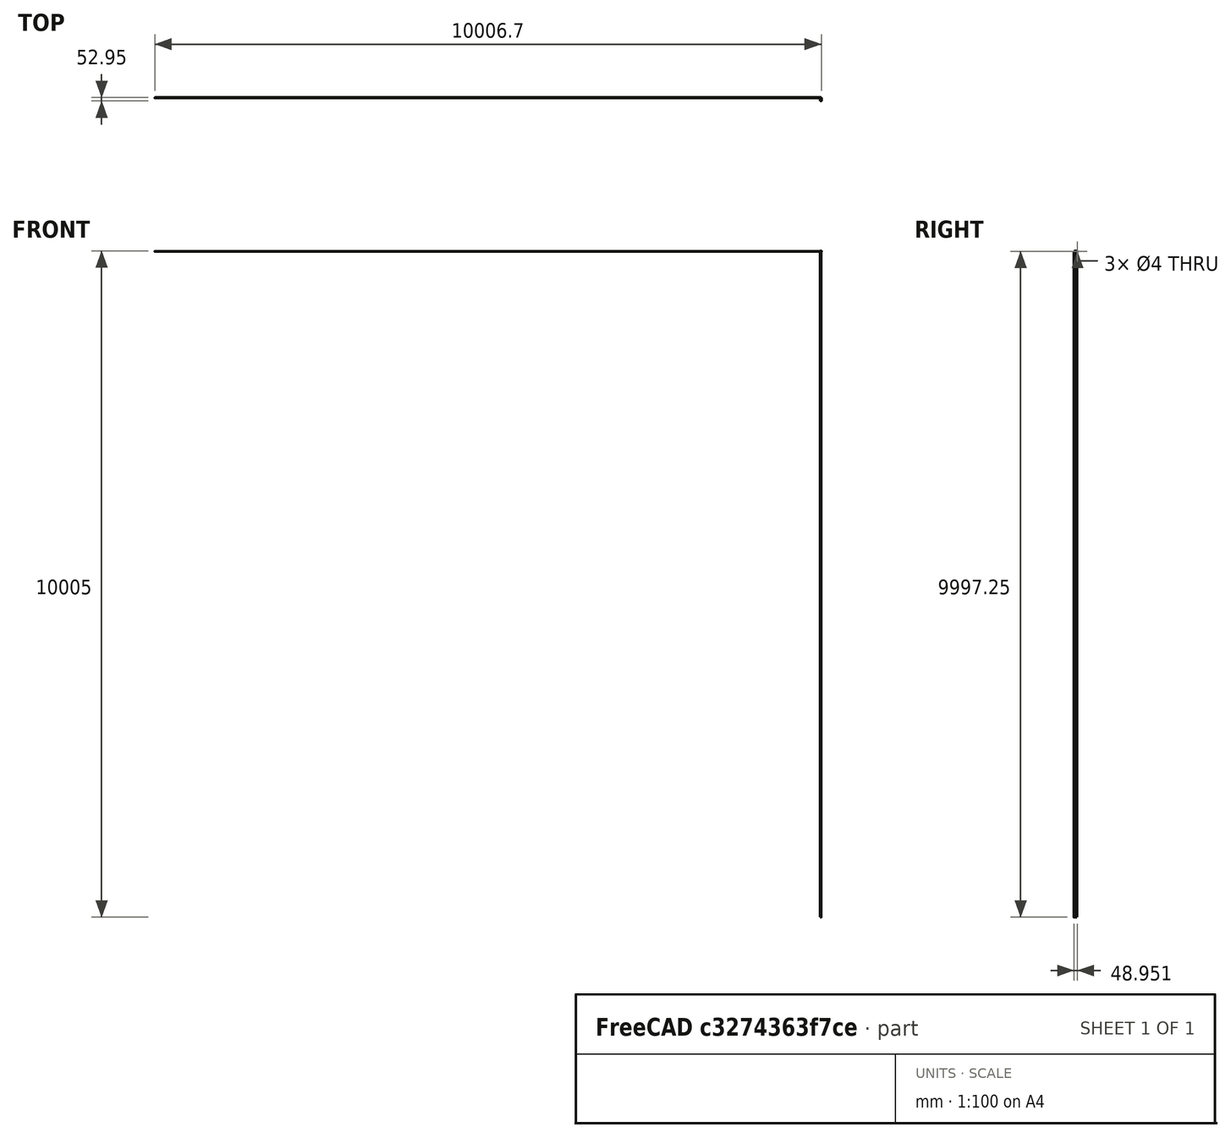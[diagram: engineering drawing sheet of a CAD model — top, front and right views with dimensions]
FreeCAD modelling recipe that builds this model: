
FCSTD DOCUMENT  (FreeCAD 0.14R3702 (Git))
Label: idler
License: CC-BY 3.0
LicenseURL: http://creativecommons.org/licenses/by/3.0/
objects: Sketcher::SketchObject×11, PartDesign::Pocket×7, PartDesign::Pad×4, PartDesign::Chamfer×2, Mesh::Feature×1, PartDesign::Fillet×1
note: 36 computed .brp shape members not serialized (recipe doc carries the construction recipe); baked Part::Feature solids carry a one-line shape summary decoded from their .brp

FEATURE [Mesh::Feature] idler1_long
  Placement = pos=(0,0,11) rot=(0,0,1;0rad)
FEATURE [Sketcher::SketchObject] Sketch
  sketch-geometry (4):
    g0: LineSegment StartX=-19.5 StartY=43.9769 StartZ=0 EndX=0 EndY=43.9769 EndZ=0
    g1: LineSegment StartX=0 StartY=43.9769 StartZ=0 EndX=0 EndY=5.97689 EndZ=0
    g2: LineSegment StartX=0 StartY=5.97689 StartZ=0 EndX=-19.5 EndY=5.97689 EndZ=0
    g3: LineSegment StartX=-19.5 StartY=5.97689 StartZ=0 EndX=-19.5 EndY=43.9769 EndZ=0
  constraints (11):
    c: Coincident(g0,g1)
    c: Coincident(g1,g2)
    c: Coincident(g2,g3)
    c: Coincident(g3,g0)
    c: Horizontal(g0)
    c: Horizontal(g2)
    c: Vertical(g1)
    c: Vertical(g3)
    c: PointOnObject(g0,g-2)
    c: DistanceY(g3) = 38
    c: DistanceX(g0) = 19.5
FEATURE [PartDesign::Pad] Pad
  Length = 8.5
  Length2 = 100
  Sketch = -> Sketch
  Type = 0
FEATURE [Sketcher::SketchObject] Sketch001
  Placement = pos=(0,0,8.5) rot=(0,0,1;0rad)
  Support = -> Pad [Face6]
  sketch-geometry (4):
    g0: LineSegment StartX=-15 StartY=41.4603 StartZ=0 EndX=-5 EndY=41.4603 EndZ=0
    g1: LineSegment StartX=-5 StartY=41.4603 StartZ=0 EndX=-5 EndY=18.4941 EndZ=0
    g2: LineSegment StartX=-5 StartY=18.4941 StartZ=0 EndX=-15 EndY=18.4941 EndZ=0
    g3: LineSegment StartX=-15 StartY=18.4941 StartZ=0 EndX=-15 EndY=41.4603 EndZ=0
  constraints (10):
    c: Coincident(g0,g1)
    c: Coincident(g1,g2)
    c: Coincident(g2,g3)
    c: Coincident(g3,g0)
    c: Horizontal(g0)
    c: Horizontal(g2)
    c: Vertical(g1)
    c: Vertical(g3)
    c: DistanceX(g0) = -5
    c: DistanceX(g0) = 10
FEATURE [PartDesign::Pocket] Pocket
  Length = 5
  Sketch = -> Sketch001
  Type = 1
FEATURE [Sketcher::SketchObject] Sketch002
  Placement = pos=(0,0,8.5) rot=(0,0,1;0rad)
  Support = -> Pocket [Face5]
  sketch-geometry (4):
    g0: LineSegment StartX=-19.9255 StartY=18.8051 StartZ=0 EndX=0.686893 EndY=18.8051 EndZ=0
    g1: LineSegment StartX=0.686893 StartY=18.8051 StartZ=0 EndX=0.686893 EndY=5.03095 EndZ=0
    g2: LineSegment StartX=0.686893 StartY=5.03095 StartZ=0 EndX=-19.9255 EndY=5.03095 EndZ=0
    g3: LineSegment StartX=-19.9255 StartY=5.03095 StartZ=0 EndX=-19.9255 EndY=18.8051 EndZ=0
  constraints (8):
    c: Coincident(g0,g1)
    c: Coincident(g1,g2)
    c: Coincident(g2,g3)
    c: Coincident(g3,g0)
    c: Horizontal(g0)
    c: Horizontal(g2)
    c: Vertical(g1)
    c: Vertical(g3)
FEATURE [PartDesign::Pocket] Pocket001
  Length = 1.5
  Sketch = -> Sketch002
  Type = 0
FEATURE [Sketcher::SketchObject] Sketch003
  Placement = pos=(0,0,7) rot=(0,0,1;0rad)
  Support = -> Pocket001 [Face7]
  sketch-geometry (4):
    g0: ArcOfCircle CenterX=-5.11958 CenterY=13.125 CenterZ=0 NormalX=0 NormalY=0 NormalZ=1 Radius=2.6 StartAngle=1.234e-08 EndAngle=3.14159
    g1: ArcOfCircle CenterX=-5.11958 CenterY=1.62771 CenterZ=0 NormalX=0 NormalY=0 NormalZ=1 Radius=2.6 StartAngle=3.14159 EndAngle=6.28319
    g2: LineSegment StartX=-7.71958 StartY=13.125 StartZ=0 EndX=-7.71958 EndY=1.62771 EndZ=0
    g3: LineSegment StartX=-2.51958 StartY=13.125 StartZ=0 EndX=-2.51958 EndY=1.62771 EndZ=0
  constraints (11):
    c: Tangent(g0,g2)
    c: Tangent(g0,g3)
    c: Tangent(g1,g2)
    c: Tangent(g1,g3)
    c: Coincident(g0,g3)
    c: Coincident(g0,g2)
    c: Coincident(g2,g1)
    c: Coincident(g3,g1)
    c: Vertical(g2)
    c: Equal(g0,g1)
    c: Radius(g1) = 2.6
FEATURE [PartDesign::Pocket] Pocket002
  Length = 5
  Sketch = -> Sketch003
  Type = 1
FEATURE [Sketcher::SketchObject] Sketch004
  Placement = pos=(0,43.9769,0) rot=(0,0.707107,0.707107;3.14159rad)
  Support = -> Pocket002 [Face1]
  sketch-geometry (4):
    g0: LineSegment StartX=6 StartY=8.5 StartZ=0 EndX=10.5 EndY=8.5 EndZ=0
    g1: LineSegment StartX=10.5 StartY=8.5 StartZ=0 EndX=10.5 EndY=0 EndZ=0
    g2: LineSegment StartX=10.5 StartY=0 StartZ=0 EndX=6 EndY=0 EndZ=0
    g3: LineSegment StartX=6 StartY=0 StartZ=0 EndX=6 EndY=8.5 EndZ=0
  constraints (11):
    c: Coincident(g0,g1)
    c: Coincident(g1,g2)
    c: Coincident(g2,g3)
    c: Coincident(g3,g0)
    c: Horizontal(g0)
    c: Horizontal(g2)
    c: Vertical(g1)
    c: Vertical(g3)
    c: PointOnObject(g1,g-1)
    c: DistanceX(g0) = 4.5
    c: DistanceX(g0) = 6
FEATURE [PartDesign::Pad] Pad001
  Length = 8
  Length2 = 100
  Sketch = -> Sketch004
  Type = 0
FEATURE [Sketcher::SketchObject] Sketch005
  ExternalGeometry = -> [Pad001]
  Placement = pos=(-6,0,0) rot=(0.57735,0.57735,0.57735;2.0944rad)
  Support = -> Pad001 [Face23]
  sketch-geometry (1):
    g0: Circle CenterX=47.9813 CenterY=4.25 CenterZ=0 NormalX=0 NormalY=0 NormalZ=1 Radius=2
  constraints (2):
    c: Radius(g0) = 2
    c: Distance(g0,g-3) = 4.25
FEATURE [PartDesign::Pocket] Pocket003
  Length = 5
  Sketch = -> Sketch005
  Type = 1
FEATURE [Sketcher::SketchObject] Sketch006
  Placement = pos=(0,0,0) rot=(0.57735,0.57735,0.57735;2.0944rad)
  Support = -> Pocket003 [Face11]
  sketch-geometry (2):
    g0: ArcOfCircle CenterX=30 CenterY=4 CenterZ=0 NormalX=0 NormalY=0 NormalZ=1 Radius=8 StartAngle=5.75959 EndAngle=9.94838
    g1: LineSegment StartX=23.0718 StartY=0 StartZ=0 EndX=36.9282 EndY=0 EndZ=0
  constraints (7):
    c: Radius(g0) = 8
    c: DistanceX(g0) = 30
    c: DistanceY(g0) = 4
    c: Coincident(g1,g0)
    c: Coincident(g1,g0)
    c: PointOnObject(g0,g-1)
    c: PointOnObject(g0,g-1)
FEATURE [PartDesign::Pad] Pad002
  Length = 6.4
  Length2 = 100
  Reversed = true
  Sketch = -> Sketch006
  Type = 0
FEATURE [Sketcher::SketchObject] Sketch007
  Placement = pos=(-19.5,0,0) rot=(0.57735,-0.57735,-0.57735;2.0944rad)
  Support = -> Pad002 [Face1]
  sketch-geometry (2):
    g0: ArcOfCircle CenterX=-30 CenterY=4 CenterZ=0 NormalX=0 NormalY=0 NormalZ=1 Radius=8 StartAngle=5.75959 EndAngle=9.94838
    g1: LineSegment StartX=-36.9282 StartY=0 StartZ=0 EndX=-23.0718 EndY=0 EndZ=0
  constraints (7):
    c: Radius(g0) = 8
    c: DistanceX(g0) = -30
    c: DistanceY(g0) = 4
    c: Coincident(g1,g0)
    c: Coincident(g1,g0)
    c: PointOnObject(g0,g-1)
    c: PointOnObject(g0,g-1)
FEATURE [PartDesign::Pad] Pad003
  Length = 6
  Length2 = 100
  Reversed = true
  Sketch = -> Sketch007
  Type = 0
FEATURE [Sketcher::SketchObject] Sketch008
  Placement = pos=(-13.5,0,0) rot=(0.57735,0.57735,0.57735;2.0944rad)
  Support = -> Pad003 [Face22]
  sketch-geometry (5):
    g0: ArcOfCircle CenterX=30 CenterY=4.25 CenterZ=0 NormalX=0 NormalY=0 NormalZ=1 Radius=4 StartAngle=5.83037 EndAngle=9.87759
    g1: LineSegment [constr] StartX=33.5969 StartY=2.5 StartZ=0 EndX=26.4031 EndY=2.5 EndZ=0
    g2: LineSegment StartX=26.4031 StartY=2.5 StartZ=0 EndX=24.6526 EndY=0 EndZ=0
    g3: LineSegment StartX=24.6526 StartY=0 StartZ=0 EndX=35.3474 EndY=0 EndZ=0
    g4: LineSegment StartX=35.3474 StartY=0 StartZ=0 EndX=33.5969 EndY=2.5 EndZ=0
  constraints (15):
    c: DistanceY(g0) = 4.25
    c: DistanceX(g0) = 30
    c: Coincident(g1,g0)
    c: Coincident(g1,g0)
    c: Horizontal(g1)
    c: Radius(g0) = 4
    c: Coincident(g0,g2)
    c: PointOnObject(g2,g-1)
    c: Coincident(g2,g3)
    c: Horizontal(g3)
    c: Coincident(g3,g4)
    c: Coincident(g4,g0)
    c: Angle(g1,g4) = 2.18166
    c: Angle(g2,g1) = 2.18166
    c: Distance(g0,g3) = 2.5
FEATURE [PartDesign::Pocket] Pocket004
  Length = 4.5
  Sketch = -> Sketch008
  Type = 0
FEATURE [Sketcher::SketchObject] Sketch009
  Placement = pos=(-6.4,0,0) rot=(0.57735,-0.57735,-0.57735;2.0944rad)
  Support = -> Pocket004 [Face43]
  sketch-geometry (5):
    g0: ArcOfCircle CenterX=-30 CenterY=4.25 CenterZ=0 NormalX=0 NormalY=0 NormalZ=1 Radius=4 StartAngle=5.83037 EndAngle=9.87759
    g1: LineSegment [constr] StartX=-26.4031 StartY=2.5 StartZ=0 EndX=-33.5969 EndY=2.5 EndZ=0
    g2: LineSegment StartX=-33.5969 StartY=2.5 StartZ=0 EndX=-35.3474 EndY=0 EndZ=0
    g3: LineSegment StartX=-35.3474 StartY=0 StartZ=0 EndX=-24.6526 EndY=0 EndZ=0
    g4: LineSegment StartX=-24.6526 StartY=0 StartZ=0 EndX=-26.4031 EndY=2.5 EndZ=0
  constraints (15):
    c: DistanceY(g0) = 4.25
    c: DistanceX(g0) = -30
    c: Coincident(g1,g0)
    c: Coincident(g1,g0)
    c: Horizontal(g1)
    c: Radius(g0) = 4
    c: Coincident(g0,g2)
    c: PointOnObject(g2,g-1)
    c: Coincident(g2,g3)
    c: Horizontal(g3)
    c: Coincident(g3,g4)
    c: Coincident(g4,g0)
    c: Angle(g2,g1) = 2.18166
    c: Angle(g1,g4) = 2.18166
    c: Distance(g0,g3) = 2.5
FEATURE [PartDesign::Pocket] Pocket005
  Length = 4.5
  Sketch = -> Sketch009
  Type = 0
FEATURE [PartDesign::Chamfer] Chamfer
  Base = -> Pocket005 [Edge45,Edge1]
  Size = 1.49
FEATURE [PartDesign::Fillet] Fillet
  Base = -> Chamfer [Edge107,Edge140]
  Radius = 4.249
FEATURE [PartDesign::Chamfer] Chamfer001
  Base = -> Fillet [Edge42,Edge54]
  Size = 1.39
FEATURE [Sketcher::SketchObject] Sketch010
  ExternalGeometry = -> [Chamfer001]
  Placement = pos=(0,0,7) rot=(0,0,1;0rad)
  Support = -> Chamfer001 [Face17]
  sketch-geometry (1):
    g0: Circle CenterX=-5.11958 CenterY=13.125 CenterZ=0 NormalX=0 NormalY=0 NormalZ=1 Radius=4.6
  constraints (2):
    c: Coincident(g0,g-3)
    c: Radius(g0) = 4.6
FEATURE [PartDesign::Pocket] Pocket006
  Length = 1.5
  Sketch = -> Sketch010
  Type = 0
